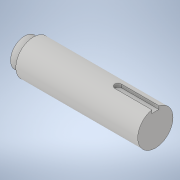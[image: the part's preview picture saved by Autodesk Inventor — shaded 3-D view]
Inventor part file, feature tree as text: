
AUTODESK INVENTOR PART (.ipt)
format: ipt  version: 2021 (Build 250183000, 183)  size: 124,416 bytes
history: native  units: in
note: dims shown in document units (in); Inventor stores cm internally (conversion verified against a paired STEP export)
features: extrude x4, sketch x4, plane x1
ambient origin geometry x8: Origin, YZ Plane, XZ Plane, XY Plane, X Axis, Y Axis, Z Axis, Center Point
bodies: Solid1 (feature_tree)
feature tree (9):
  extrude  "Extrusion1"  Depth=4.634in TaperAngle=0.0deg
  plane  "Work Plane1"
  extrude  "Extrusion9"  Depth=0.25in
  extrude  "Extrusion10"  Depth=0.125in TaperAngle=0.0deg
  extrude  "Extrusion11"  Depth=0.3125in TaperAngle=0.0deg
  sketch  "Sketch1"  dims[d0=1.25in d1=4.634in d2=0.0in]
  sketch  "Sketch9"  dims[d11=-2.0535in d26=0.25in]
  sketch  "Sketch10"  dims[d27=0.125in d28=1.313in d29=0.0in]
  sketch  "Sketch11"  dims[d30=1.0in d31=0.3125in d32=0.0in d33=1.0in d34=0.0in]
